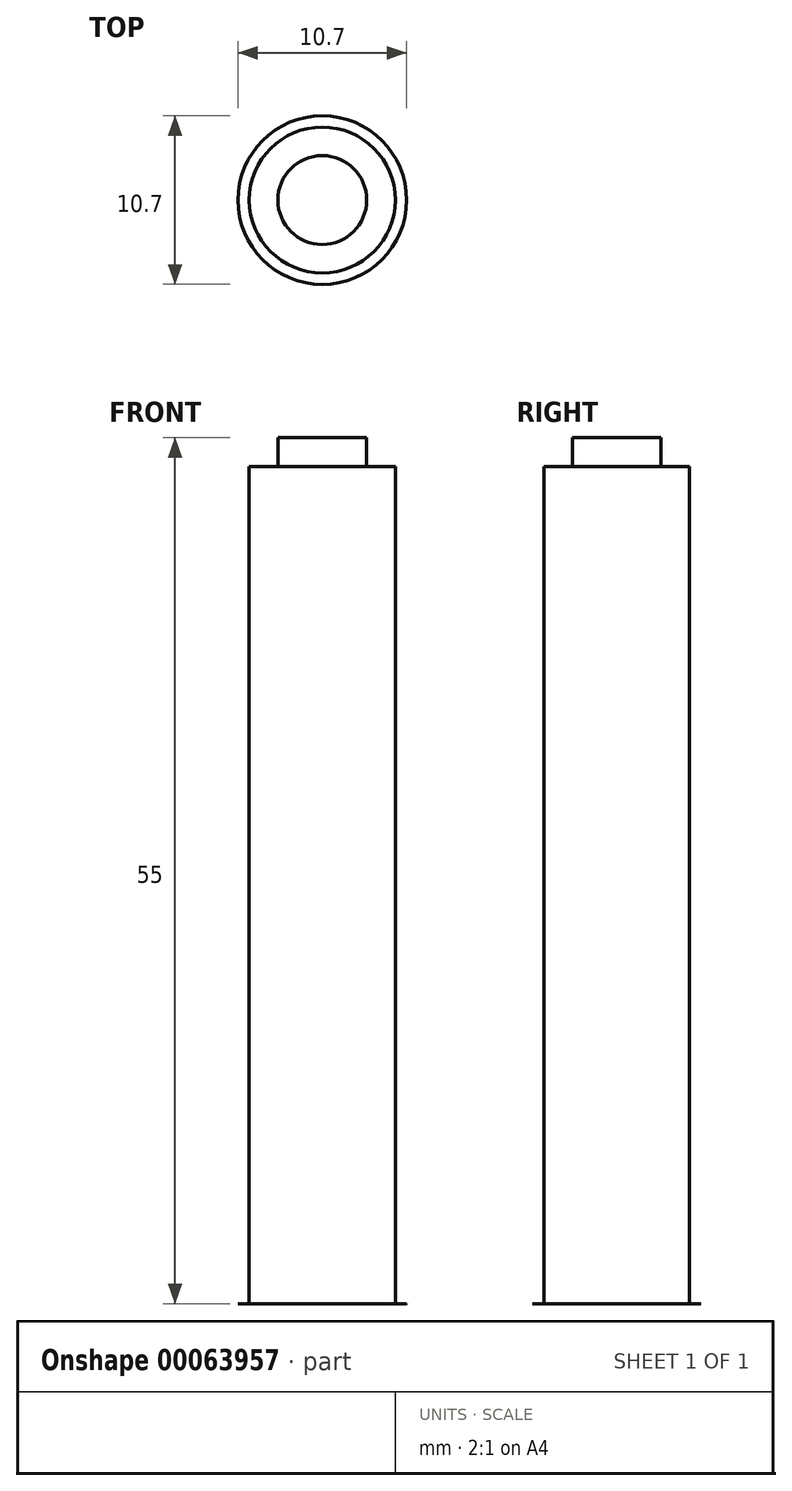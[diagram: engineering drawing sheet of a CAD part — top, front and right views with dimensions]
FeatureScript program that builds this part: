
annotation { "Feature Type Name" : "Feature", "Feature Type Description" : "" }
export const myFeature = defineFeature(function(context is Context, id is Id, definition is map)
    precondition{}
    {
        {
            var Q0;
            Q0=qCreatedBy(makeId("Top.planeOp"),FACE);
            var sketch = newSketch(context, id + "F0", { "sketchPlane" : qUnion([Q0])});
            skCircle(sketch, "E0", {"center": v(0, 0) * mm, "radius": 6.35 * mm});
            skSolve(sketch);
        }
        {
            var Q0;
            Q0 = qSketchRegion(id + "F0", true);
            extrude(context, id + "F1", {"entities" : qUnion([Q0]), "depth" : 1 / 203.2 * mm});
        }
        {
            var Q0;
            Q0=makeQuery(id+"F1.opExtrude","CAP_FACE",FACE,{"disambiguationData":[OSD([sQuery(id+"F0.wireOp",EDGE,"E0")])],"isStart":false});
            var sketch = newSketch(context, id + "F2", { "sketchPlane" : qUnion([Q0])});
            skCircle(sketch, "E1", {"center": v(0, 0) * mm, "radius": 4.64 * mm});
            skSolve(sketch);
        }
        {
            var Q0;
            Q0=makeQuery(id+"F2.imprint","IMPRINT",FACE,{"disambiguationData":[TD([[makeQuery(id+"F2.imprint","IMPRINT",EDGE,{"derivedFrom":sQuery(id+"F2.wireOp",EDGE,"E1")}),1.0]])]});
            extrude(context, id + "F3", {"entities" : qUnion([Q0]), "operationType" : NewBodyOperationType.ADD, "depth" : 55 * mm});
        }
        {
            var Q0;
            Q0=qCreatedBy(makeId("Right.planeOp"),FACE);
            var sketch = newSketch(context, id + "F4", { "sketchPlane" : qUnion([Q0])});
            skLineSegment(sketch, "E2", {"start": v(-4.82, 56.17) * mm, "end": v(-4.82, 53.17) * mm});
            skLineSegment(sketch, "E3", {"start": v(-4.82, 53.17) * mm, "end": v(-2.82, 53.17) * mm});
            skLineSegment(sketch, "E4", {"start": v(-2.82, 53.17) * mm, "end": v(-2.82, 55.02) * mm});
            skLineSegment(sketch, "E5", {"start": v(-2.82, 55.02) * mm, "end": v(-4.82, 56.17) * mm});
            skSolve(sketch);
        }
        {
            var Q0;
            Q0 = qSketchRegion(id + "F4", true);
            var Q1;
            Q1=makeQuery(id+"F3.opExtrude","CAP_EDGE",EDGE,{"disambiguationData":[OSD([sQuery(id+"F2.wireOp",EDGE,"E1")])],"isStart":false});
            revolve(context, id + "F5", {"operationType" : NewBodyOperationType.REMOVE, "entities" : qUnion([Q0]), "axis" : qUnion([Q1]), "revolveType" : RevolveType.FULL, "oppositeDirection" : true});
        }
        {
            var Q0;
            Q0=makeQuery(id+"F1.opExtrude","CAP_EDGE",EDGE,{"disambiguationData":[OSD([sQuery(id+"F0.wireOp",EDGE,"E0")])],"isStart":true});
            chamfer(context, id + "F6", {"entities" : qUnion([Q0]), "width" : 1 * mm, "tangentPropagation" : true});
        }
    });
